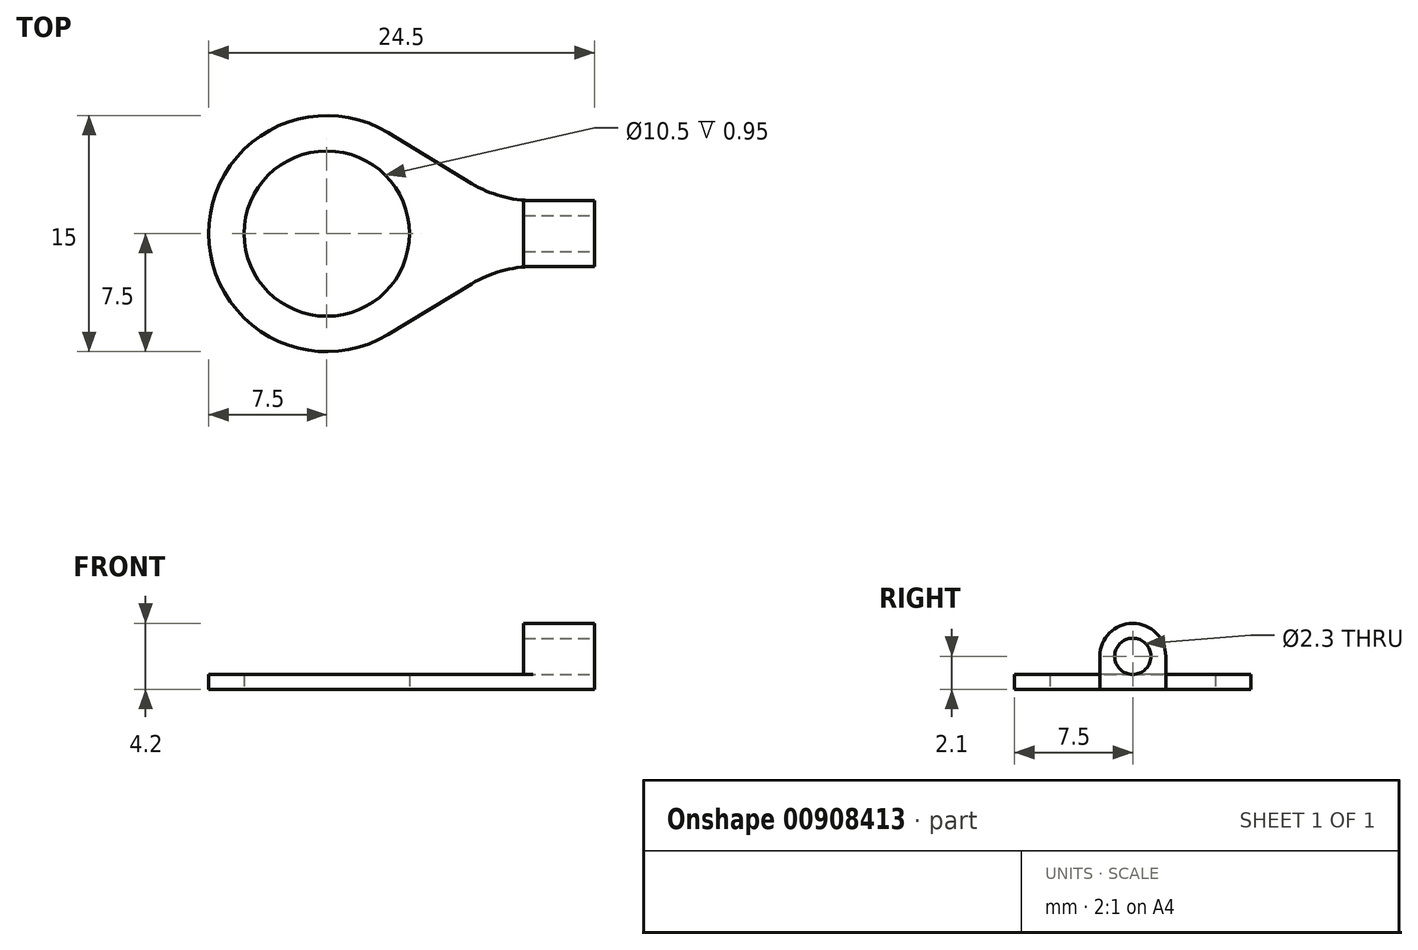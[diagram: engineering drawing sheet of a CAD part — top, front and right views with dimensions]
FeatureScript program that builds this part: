
annotation { "Feature Type Name" : "Feature", "Feature Type Description" : "" }
export const myFeature = defineFeature(function(context is Context, id is Id, definition is map)
    precondition{}
    {
        {
            var Q0;
            Q0=qCreatedBy(makeId("Top.planeOp"),FACE);
            var sketch = newSketch(context, id + "F0", { "sketchPlane" : qUnion([Q0])});
            skLineSegment(sketch, "E0.left", {"start": v(0, 7.5) * mm, "end": v(0, 7.5) * mm});
            skLineSegment(sketch, "E0.right", {"start": v(24.5, 5.4) * mm, "end": v(24.5, 9.6) * mm});
            skPoint(sketch, "E1.visualSharp", {"position": v(0, 15) * mm});
            skArc(sketch, "E1.filletArc", {"start": v(7.5, 15) * mm, "mid": v(2.2, 12.8) * mm, "end": v(0, 7.5) * mm});
            skPoint(sketch, "E2.visualSharp", {"position": v(0, 0) * mm});
            skArc(sketch, "E2.filletArc", {"start": v(0, 7.5) * mm, "mid": v(2.2, 2.2) * mm, "end": v(7.5, 0) * mm});
            skLineSegment(sketch, "E3.bottom", {"start": v(24.5, 5.4) * mm, "end": v(20.6, 5.4) * mm});
            skLineSegment(sketch, "E3.top", {"start": v(24.5, 9.6) * mm, "end": v(20.6, 9.6) * mm});
            skPoint(sketch, "E3.middle", {"position": v(24.5, 7.5) * mm});
            skArc(sketch, "E4", {"start": v(11.39, 13.91) * mm, "mid": v(0, 7.5) * mm, "end": v(11.39, 1.09) * mm});
            skCircle(sketch, "E5", {"center": v(7.5, 7.5) * mm, "radius": 5.25 * mm});
            skLineSegment(sketch, "E6", {"start": v(16.7, 10.69) * mm, "end": v(11.39, 13.91) * mm});
            skLineSegment(sketch, "E7", {"start": v(11.39, 1.09) * mm, "end": v(16.7, 4.31) * mm});
            skPoint(sketch, "E8.visualSharp", {"position": v(18.5, 9.6) * mm});
            skArc(sketch, "E8.filletArc", {"start": v(16.7, 10.69) * mm, "mid": v(18.58, 9.88) * mm, "end": v(20.6, 9.6) * mm});
            skPoint(sketch, "E9.visualSharp", {"position": v(18.5, 5.4) * mm});
            skArc(sketch, "E9.filletArc", {"start": v(20.6, 5.4) * mm, "mid": v(18.58, 5.12) * mm, "end": v(16.7, 4.31) * mm});
            skPoint(sketch, "E10.orphan", {"position": v(29, 9.6) * mm});
            skPoint(sketch, "E11.orphan", {"position": v(29, 5.4) * mm});
            skPoint(sketch, "E0.top.end.orphan", {"position": v(24.5, 15) * mm});
            skPoint(sketch, "E0.bottom.end.orphan", {"position": v(24.5, 0) * mm});
            skPoint(sketch, "E3.right.end.orphan", {"position": v(20, 9.6) * mm});
            skPoint(sketch, "E3.right.start.orphan", {"position": v(20, 5.4) * mm});
            skSolve(sketch);
        }
        {
            var Q0;
            Q0=makeQuery(id+"F0.imprint","IMPRINT",FACE,{"disambiguationData":[TD([[makeQuery(id+"F0.imprint","IMPRINT",EDGE,{"derivedFrom":sQuery(id+"F0.wireOp",EDGE,"E0.right")}),1.0]])]});
            extrude(context, id + "F1", {"entities" : qUnion([Q0]), "depth" : 0.95 * mm, "offsetDistance" : 25 * mm});
        }
        {
            var Q0;
            Q0=makeQuery(id+"F1.opExtrude","CAP_FACE",FACE,{"disambiguationData":[OSD([sQuery(id+"F0.wireOp",EDGE,"E0.right"),sQuery(id+"F0.wireOp",EDGE,"E3.bottom"),sQuery(id+"F0.wireOp",EDGE,"E3.top"),sQuery(id+"F0.wireOp",EDGE,"E4"),sQuery(id+"F0.wireOp",EDGE,"E5"),sQuery(id+"F0.wireOp",EDGE,"E6"),sQuery(id+"F0.wireOp",EDGE,"E7"),sQuery(id+"F0.wireOp",EDGE,"E8.filletArc"),sQuery(id+"F0.wireOp",EDGE,"E9.filletArc")])],"isStart":false});
            var sketch = newSketch(context, id + "F2", { "sketchPlane" : qUnion([Q0])});
            skLineSegment(sketch, "E12.bottom", {"start": v(24.5, 9.6) * mm, "end": v(20, 9.6) * mm});
            skLineSegment(sketch, "E12.top", {"start": v(24.5, 5.4) * mm, "end": v(20, 5.4) * mm});
            skLineSegment(sketch, "E12.left", {"start": v(24.5, 9.6) * mm, "end": v(24.5, 5.4) * mm});
            skLineSegment(sketch, "E12.right", {"start": v(20, 9.6) * mm, "end": v(20, 5.4) * mm});
            skSolve(sketch);
        }
        {
            var Q0;
            {var subQ0=sQuery(id+"F2.wireOp",EDGE,"E12.left");Q0=makeQuery(id+"F2.imprint","IMPRINT",FACE,{"disambiguationData":[TD([[makeQuery(id+"F2.imprint","IMPRINT",EDGE,{"derivedFrom":subQ0}),1.0]])]});}
            extrude(context, id + "F3", {"entities" : qUnion([Q0]), "operationType" : NewBodyOperationType.ADD, "depth" : 3.25 * mm, "offsetDistance" : 25 * mm});
        }
        {
            var Q0;
            Q0=makeQuery(id+"F3.opExtrude","CAP_EDGE",EDGE,{"disambiguationData":[OSD([sQuery(id+"F2.wireOp",EDGE,"E12.bottom")])],"isStart":false});
            var Q1;
            Q1=makeQuery(id+"F3.opExtrude","CAP_EDGE",EDGE,{"disambiguationData":[OSD([sQuery(id+"F2.wireOp",EDGE,"E12.top")])],"isStart":false});
            fillet(context, id + "F4", {"entities" : qUnion([Q0, Q1]), "radius" : 2.1 * mm, "tangentPropagation" : true, "allowEdgeOverflow" : false});
        }
        {
            var Q0;
            Q0=makeQuery(id+"F3.boolean.opBoolean","MERGE",FACE,{"derivedFrom":[makeQuery(id+"F1.opExtrude","SWEPT_FACE",FACE,{"disambiguationData":[OSD([sQuery(id+"F0.wireOp",EDGE,"E0.right")])]}),makeQuery(id+"F3.opExtrude","SWEPT_FACE",FACE,{"disambiguationData":[OSD([sQuery(id+"F2.wireOp",EDGE,"E12.left")])]})]});
            var sketch = newSketch(context, id + "F5", { "sketchPlane" : qUnion([Q0])});
            skCircle(sketch, "E13", {"center": v(7.5, 2.1) * mm, "radius": 1.15 * mm});
            skSolve(sketch);
        }
        {
            var Q0;
            Q0=makeQuery(id+"F5.imprint","IMPRINT",FACE,{"disambiguationData":[TD([[makeQuery(id+"F5.imprint","IMPRINT",EDGE,{"derivedFrom":sQuery(id+"F5.wireOp",EDGE,"E13")}),1.0]])]});
            extrude(context, id + "F6", {"entities" : qUnion([Q0]), "operationType" : NewBodyOperationType.REMOVE, "oppositeDirection" : true, "depth" : 25 * mm, "offsetDistance" : 25 * mm});
        }
    });
